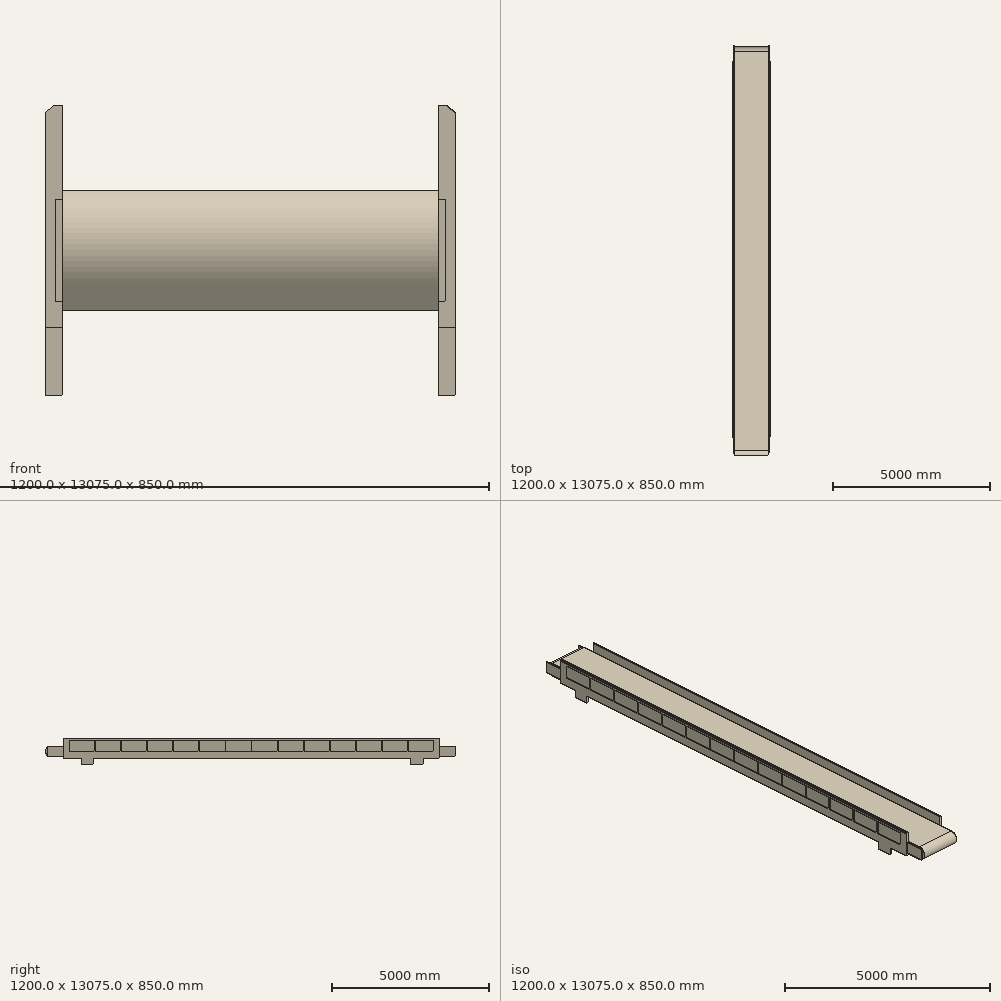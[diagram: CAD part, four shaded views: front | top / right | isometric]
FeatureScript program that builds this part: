
annotation { "Feature Type Name" : "Feature", "Feature Type Description" : "" }
export const myFeature = defineFeature(function(context is Context, id is Id, definition is map)
    precondition{}
    {
        {
            var Q0;
            Q0=qCreatedBy(makeId("Right.planeOp"),FACE);
            cPlane(context, id + "F0", {"entities" : qUnion([Q0]), "cplaneType" : CPlaneType.OFFSET, "offset" : 550 * mm, "width" : 150 * mm, "height" : 150 * mm});
        }
        {
            var Q0;
            Q0=qCreatedBy(makeId("Right.planeOp"),FACE);
            var sketch = newSketch(context, id + "F1", { "sketchPlane" : qUnion([Q0])});
            skCircle(sketch, "E0", {"center": v(0, 0) * mm, "radius": 150 * mm});
            skCircle(sketch, "E1.1.0.0", {"center": v(12700, 0) * mm, "radius": 150 * mm});
            skLineSegment(sketch, "E1.direction1", {"start": v(0, 0) * mm, "end": v(12700, 0) * mm, "construction": true});
            skSolve(sketch);
        }
        {
            var Q0;
            Q0 = qSketchRegion(id + "F1", true);
            var Q1;
            Q1 = qConstructionFilter(qBodyType(qCreatedBy(id + "F1" ,EDGE), BodyType.WIRE), ConstructionObject.NO);
            extrude(context, id + "F2", {"entities" : qUnion([Q0]), "surfaceEntities" : qUnion([Q1]), "depth" : 1100 * mm, "offsetDistance" : 25 * mm});
        }
        {
            var Q0;
            Q0=makeQuery(id+"F2.opExtrude","CAP_FACE",FACE,{"disambiguationData":[OSD([sQuery(id+"F1.wireOp",EDGE,"E0")])],"isStart":false});
            var sketch = newSketch(context, id + "F3", { "sketchPlane" : qUnion([Q0])});
            skCircle(sketch, "E2", {"center": v(0, 0) * mm, "radius": 175 * mm});
            skCircle(sketch, "E3", {"center": v(12700, 0) * mm, "radius": 175 * mm});
            skLineSegment(sketch, "E4.bottom", {"start": v(0, 175) * mm, "end": v(12700, 175) * mm});
            skLineSegment(sketch, "E4.top", {"start": v(0, -175) * mm, "end": v(12700, -175) * mm});
            skLineSegment(sketch, "E4.left", {"start": v(0, 175) * mm, "end": v(0, -175) * mm});
            skLineSegment(sketch, "E4.right", {"start": v(12700, 175) * mm, "end": v(12700, -175) * mm});
            skSolve(sketch);
        }
        {
            var Q0;
            Q0 = qSketchRegion(id + "F3", true);
            extrude(context, id + "F4", {"entities" : qUnion([Q0]), "oppositeDirection" : true, "depth" : 1100 * mm, "offsetDistance" : 25 * mm});
        }
        {
            var Q0;
            Q0=qCreatedBy(makeId("Front.planeOp"),FACE);
            var sketch = newSketch(context, id + "F5", { "sketchPlane" : qUnion([Q0])});
            skLineSegment(sketch, "E5.bottom", {"start": v(0, 425) * mm, "end": v(-25, 425) * mm});
            skLineSegment(sketch, "E5.top", {"start": v(0, -225) * mm, "end": v(-50, -225) * mm});
            skLineSegment(sketch, "E5.left", {"start": v(0, 425) * mm, "end": v(0, -225) * mm});
            skLineSegment(sketch, "E5.right", {"start": v(-50, 401.85) * mm, "end": v(-50, -225) * mm});
            skLineSegment(sketch, "E6", {"start": v(-25, 425) * mm, "end": v(-50, 401.85) * mm});
            skPoint(sketch, "E7.orphan", {"position": v(-50, 425) * mm});
            skLineSegment(sketch, "E8.MirrorCS", {"start": v(1100, 425) * mm, "end": v(1125, 425) * mm});
            skLineSegment(sketch, "E9.MirrorCS", {"start": v(1125, 425) * mm, "end": v(1150, 401.85) * mm});
            skLineSegment(sketch, "E10.MirrorCS", {"start": v(1100, -225) * mm, "end": v(1150, -225) * mm});
            skPoint(sketch, "E11.MirrorP", {"position": v(1150, 425) * mm});
            skLineSegment(sketch, "E12.MirrorCS", {"start": v(1150, 401.85) * mm, "end": v(1150, -225) * mm});
            skLineSegment(sketch, "E13.MirrorCS", {"start": v(1100, 425) * mm, "end": v(1100, -225) * mm});
            skSolve(sketch);
        }
        {
            var Q0;
            Q0 = qSketchRegion(id + "F5", true);
            extrude(context, id + "F6", {"entities" : qUnion([Q0]), "oppositeDirection" : true, "depth" : 12400 * mm, "offsetDistance" : 25 * mm, "hasSecondDirection" : true, "secondDirectionOppositeDirection" : false, "secondDirectionDepth" : -400 * mm});
        }
        {
            var Q0;
            Q0=makeQuery(id+"F6.opExtrude","CAP_FACE",FACE,{"disambiguationData":[OSD([sQuery(id+"F5.wireOp",EDGE,"E5.bottom"),sQuery(id+"F5.wireOp",EDGE,"E5.top"),sQuery(id+"F5.wireOp",EDGE,"E5.left"),sQuery(id+"F5.wireOp",EDGE,"E5.right"),sQuery(id+"F5.wireOp",EDGE,"E6")])],"isStart":true});
            var sketch = newSketch(context, id + "F7", { "sketchPlane" : qUnion([Q0])});
            skLineSegment(sketch, "E14.bottom", {"start": v(0, 150) * mm, "end": v(-20, 150) * mm});
            skLineSegment(sketch, "E14.top", {"start": v(0, -150) * mm, "end": v(-20, -150) * mm});
            skLineSegment(sketch, "E14.left", {"start": v(0, 150) * mm, "end": v(0, -150) * mm});
            skLineSegment(sketch, "E14.right", {"start": v(-20, 150) * mm, "end": v(-20, -150) * mm});
            skLineSegment(sketch, "E15.MirrorCS", {"start": v(1100, -150) * mm, "end": v(1120, -150) * mm});
            skLineSegment(sketch, "E16.MirrorCS", {"start": v(1100, 150) * mm, "end": v(1120, 150) * mm});
            skLineSegment(sketch, "E17.MirrorCS", {"start": v(1120, 150) * mm, "end": v(1120, -150) * mm});
            skLineSegment(sketch, "E18.MirrorCS", {"start": v(1100, 150) * mm, "end": v(1100, -150) * mm});
            skSolve(sketch);
        }
        {
            var Q0;
            Q0 = qSketchRegion(id + "F7", true);
            extrude(context, id + "F8", {"entities" : qUnion([Q0]), "operationType" : NewBodyOperationType.ADD, "depth" : 500 * mm, "offsetDistance" : 25 * mm, "hasSecondDirection" : true, "secondDirectionOppositeDirection" : true, "secondDirectionDepth" : 12500 * mm});
        }
        {
            var Q0;
            Q0=makeQuery(id+"F6.opExtrude","SWEPT_FACE",FACE,{"disambiguationData":[OSD([sQuery(id+"F5.wireOp",EDGE,"E5.right")])]});
            var sketch = newSketch(context, id + "F9", { "sketchPlane" : qUnion([Q0])});
            skLineSegment(sketch, "E19.bottom", {"start": v(-600, 340) * mm, "end": v(-1400, 340) * mm});
            skLineSegment(sketch, "E19.top", {"start": v(-600, 0) * mm, "end": v(-1400, 0) * mm});
            skLineSegment(sketch, "E19.left", {"start": v(-600, 340) * mm, "end": v(-600, 0) * mm});
            skLineSegment(sketch, "E19.right", {"start": v(-1400, 340) * mm, "end": v(-1400, 0) * mm});
            skLineSegment(sketch, "E20.1.0.0", {"start": v(-1430, 0) * mm, "end": v(-2230, 0) * mm});
            skLineSegment(sketch, "E20.1.0.1", {"start": v(-2230, 340) * mm, "end": v(-2230, 0) * mm});
            skLineSegment(sketch, "E20.1.0.2", {"start": v(-1430, 340) * mm, "end": v(-1430, 0) * mm});
            skLineSegment(sketch, "E20.1.0.3", {"start": v(-1430, 340) * mm, "end": v(-2230, 340) * mm});
            skLineSegment(sketch, "E20.2.0.0", {"start": v(-2260, 0) * mm, "end": v(-3060, 0) * mm});
            skLineSegment(sketch, "E20.2.0.1", {"start": v(-3060, 340) * mm, "end": v(-3060, 0) * mm});
            skLineSegment(sketch, "E20.2.0.2", {"start": v(-2260, 340) * mm, "end": v(-2260, 0) * mm});
            skLineSegment(sketch, "E20.2.0.3", {"start": v(-2260, 340) * mm, "end": v(-3060, 340) * mm});
            skLineSegment(sketch, "E20.3.0.0", {"start": v(-3090, 0) * mm, "end": v(-3890, 0) * mm});
            skLineSegment(sketch, "E20.3.0.1", {"start": v(-3890, 340) * mm, "end": v(-3890, 0) * mm});
            skLineSegment(sketch, "E20.3.0.2", {"start": v(-3090, 340) * mm, "end": v(-3090, 0) * mm});
            skLineSegment(sketch, "E20.3.0.3", {"start": v(-3090, 340) * mm, "end": v(-3890, 340) * mm});
            skLineSegment(sketch, "E20.4.0.0", {"start": v(-3920, 0) * mm, "end": v(-4720, 0) * mm});
            skLineSegment(sketch, "E20.4.0.1", {"start": v(-4720, 340) * mm, "end": v(-4720, 0) * mm});
            skLineSegment(sketch, "E20.4.0.2", {"start": v(-3920, 340) * mm, "end": v(-3920, 0) * mm});
            skLineSegment(sketch, "E20.4.0.3", {"start": v(-3920, 340) * mm, "end": v(-4720, 340) * mm});
            skLineSegment(sketch, "E20.5.0.0", {"start": v(-4750, 0) * mm, "end": v(-5550, 0) * mm});
            skLineSegment(sketch, "E20.5.0.1", {"start": v(-5550, 340) * mm, "end": v(-5550, 0) * mm});
            skLineSegment(sketch, "E20.5.0.2", {"start": v(-4750, 340) * mm, "end": v(-4750, 0) * mm});
            skLineSegment(sketch, "E20.5.0.3", {"start": v(-4750, 340) * mm, "end": v(-5550, 340) * mm});
            skLineSegment(sketch, "E20.6.0.0", {"start": v(-5580, 0) * mm, "end": v(-6380, 0) * mm});
            skLineSegment(sketch, "E20.6.0.1", {"start": v(-6380, 340) * mm, "end": v(-6380, 0) * mm});
            skLineSegment(sketch, "E20.6.0.2", {"start": v(-5580, 340) * mm, "end": v(-5580, 0) * mm});
            skLineSegment(sketch, "E20.6.0.3", {"start": v(-5580, 340) * mm, "end": v(-6380, 340) * mm});
            skLineSegment(sketch, "E20.7.0.0", {"start": v(-6410, 0) * mm, "end": v(-7210, 0) * mm});
            skLineSegment(sketch, "E20.7.0.1", {"start": v(-7210, 340) * mm, "end": v(-7210, 0) * mm});
            skLineSegment(sketch, "E20.7.0.2", {"start": v(-6410, 340) * mm, "end": v(-6410, 0) * mm});
            skLineSegment(sketch, "E20.7.0.3", {"start": v(-6410, 340) * mm, "end": v(-7210, 340) * mm});
            skLineSegment(sketch, "E20.8.0.0", {"start": v(-7240, 0) * mm, "end": v(-8040, 0) * mm});
            skLineSegment(sketch, "E20.8.0.1", {"start": v(-8040, 340) * mm, "end": v(-8040, 0) * mm});
            skLineSegment(sketch, "E20.8.0.2", {"start": v(-7240, 340) * mm, "end": v(-7240, 0) * mm});
            skLineSegment(sketch, "E20.8.0.3", {"start": v(-7240, 340) * mm, "end": v(-8040, 340) * mm});
            skLineSegment(sketch, "E20.9.0.0", {"start": v(-8070, 0) * mm, "end": v(-8870, 0) * mm});
            skLineSegment(sketch, "E20.9.0.1", {"start": v(-8870, 340) * mm, "end": v(-8870, 0) * mm});
            skLineSegment(sketch, "E20.9.0.2", {"start": v(-8070, 340) * mm, "end": v(-8070, 0) * mm});
            skLineSegment(sketch, "E20.9.0.3", {"start": v(-8070, 340) * mm, "end": v(-8870, 340) * mm});
            skLineSegment(sketch, "E20.10.0.0", {"start": v(-8900, 0) * mm, "end": v(-9700, 0) * mm});
            skLineSegment(sketch, "E20.10.0.1", {"start": v(-9700, 340) * mm, "end": v(-9700, 0) * mm});
            skLineSegment(sketch, "E20.10.0.2", {"start": v(-8900, 340) * mm, "end": v(-8900, 0) * mm});
            skLineSegment(sketch, "E20.10.0.3", {"start": v(-8900, 340) * mm, "end": v(-9700, 340) * mm});
            skLineSegment(sketch, "E20.11.0.0", {"start": v(-9730, 0) * mm, "end": v(-10530, 0) * mm});
            skLineSegment(sketch, "E20.11.0.1", {"start": v(-10530, 340) * mm, "end": v(-10530, 0) * mm});
            skLineSegment(sketch, "E20.11.0.2", {"start": v(-9730, 340) * mm, "end": v(-9730, 0) * mm});
            skLineSegment(sketch, "E20.11.0.3", {"start": v(-9730, 340) * mm, "end": v(-10530, 340) * mm});
            skLineSegment(sketch, "E20.12.0.0", {"start": v(-10560, 0) * mm, "end": v(-11360, 0) * mm});
            skLineSegment(sketch, "E20.12.0.1", {"start": v(-11360, 340) * mm, "end": v(-11360, 0) * mm});
            skLineSegment(sketch, "E20.12.0.2", {"start": v(-10560, 340) * mm, "end": v(-10560, 0) * mm});
            skLineSegment(sketch, "E20.12.0.3", {"start": v(-10560, 340) * mm, "end": v(-11360, 340) * mm});
            skLineSegment(sketch, "E20.13.0.0", {"start": v(-11390, 0) * mm, "end": v(-12190, 0) * mm});
            skLineSegment(sketch, "E20.13.0.1", {"start": v(-12190, 340) * mm, "end": v(-12190, 0) * mm});
            skLineSegment(sketch, "E20.13.0.2", {"start": v(-11390, 340) * mm, "end": v(-11390, 0) * mm});
            skLineSegment(sketch, "E20.13.0.3", {"start": v(-11390, 340) * mm, "end": v(-12190, 340) * mm});
            skLineSegment(sketch, "E20.direction1", {"start": v(-1400, 0) * mm, "end": v(-2230, 0) * mm, "construction": true});
            skSolve(sketch);
        }
        {
            var Q0;
            Q0 = qSketchRegion(id + "F9", true);
            extrude(context, id + "F10", {"entities" : qUnion([Q0]), "operationType" : NewBodyOperationType.REMOVE, "oppositeDirection" : true, "depth" : 10 * mm, "offsetDistance" : 25 * mm});
        }
        {
            var Q0;
            Q0=makeQuery(id+"F6.opExtrude","SWEPT_FACE",FACE,{"disambiguationData":[OSD([sQuery(id+"F5.wireOp",EDGE,"E12.MirrorCS")])]});
            var sketch = newSketch(context, id + "F11", { "sketchPlane" : qUnion([Q0])});
            skLineSegment(sketch, "E21.0.0", {"start": v(1400, 0) * mm, "end": v(600, 0) * mm});
            skLineSegment(sketch, "E21.0.1", {"start": v(600, 0) * mm, "end": v(600, 340) * mm});
            skLineSegment(sketch, "E21.0.2", {"start": v(600, 340) * mm, "end": v(1400, 340) * mm});
            skLineSegment(sketch, "E21.0.3", {"start": v(1400, 340) * mm, "end": v(1400, 0) * mm});
            skLineSegment(sketch, "E22.0.0", {"start": v(1430, 0) * mm, "end": v(1430, 340) * mm});
            skLineSegment(sketch, "E22.0.1", {"start": v(1430, 340) * mm, "end": v(2230, 340) * mm});
            skLineSegment(sketch, "E22.0.2", {"start": v(2230, 340) * mm, "end": v(2230, 0) * mm});
            skLineSegment(sketch, "E22.0.3", {"start": v(2230, 0) * mm, "end": v(1430, 0) * mm});
            skLineSegment(sketch, "E23.0.0", {"start": v(2260, 0) * mm, "end": v(2260, 340) * mm});
            skLineSegment(sketch, "E23.0.1", {"start": v(2260, 340) * mm, "end": v(3060, 340) * mm});
            skLineSegment(sketch, "E23.0.2", {"start": v(3060, 340) * mm, "end": v(3060, 0) * mm});
            skLineSegment(sketch, "E23.0.3", {"start": v(3060, 0) * mm, "end": v(2260, 0) * mm});
            skLineSegment(sketch, "E24.0.0", {"start": v(3090, 0) * mm, "end": v(3090, 340) * mm});
            skLineSegment(sketch, "E24.0.1", {"start": v(3090, 340) * mm, "end": v(3890, 340) * mm});
            skLineSegment(sketch, "E24.0.2", {"start": v(3890, 340) * mm, "end": v(3890, 0) * mm});
            skLineSegment(sketch, "E24.0.3", {"start": v(3890, 0) * mm, "end": v(3090, 0) * mm});
            skLineSegment(sketch, "E25.0.0", {"start": v(3920, 0) * mm, "end": v(3920, 340) * mm});
            skLineSegment(sketch, "E25.0.1", {"start": v(3920, 340) * mm, "end": v(4720, 340) * mm});
            skLineSegment(sketch, "E25.0.2", {"start": v(4720, 340) * mm, "end": v(4720, 0) * mm});
            skLineSegment(sketch, "E25.0.3", {"start": v(4720, 0) * mm, "end": v(3920, 0) * mm});
            skLineSegment(sketch, "E26.0.0", {"start": v(4750, 0) * mm, "end": v(4750, 340) * mm});
            skLineSegment(sketch, "E26.0.1", {"start": v(4750, 340) * mm, "end": v(5550, 340) * mm});
            skLineSegment(sketch, "E26.0.2", {"start": v(5550, 340) * mm, "end": v(5550, 0) * mm});
            skLineSegment(sketch, "E26.0.3", {"start": v(5550, 0) * mm, "end": v(4750, 0) * mm});
            skLineSegment(sketch, "E27.0.0", {"start": v(5580, 0) * mm, "end": v(5580, 340) * mm});
            skLineSegment(sketch, "E27.0.1", {"start": v(5580, 340) * mm, "end": v(6380, 340) * mm});
            skLineSegment(sketch, "E27.0.2", {"start": v(6380, 340) * mm, "end": v(6380, 0) * mm});
            skLineSegment(sketch, "E27.0.3", {"start": v(6380, 0) * mm, "end": v(5580, 0) * mm});
            skLineSegment(sketch, "E28.0.0", {"start": v(6410, 0) * mm, "end": v(6410, 340) * mm});
            skLineSegment(sketch, "E28.0.1", {"start": v(6410, 340) * mm, "end": v(7210, 340) * mm});
            skLineSegment(sketch, "E28.0.2", {"start": v(7210, 340) * mm, "end": v(7210, 0) * mm});
            skLineSegment(sketch, "E28.0.3", {"start": v(7210, 0) * mm, "end": v(6410, 0) * mm});
            skLineSegment(sketch, "E29.0.0", {"start": v(7240, 0) * mm, "end": v(7240, 340) * mm});
            skLineSegment(sketch, "E29.0.1", {"start": v(7240, 340) * mm, "end": v(8040, 340) * mm});
            skLineSegment(sketch, "E29.0.2", {"start": v(8040, 340) * mm, "end": v(8040, 0) * mm});
            skLineSegment(sketch, "E29.0.3", {"start": v(8040, 0) * mm, "end": v(7240, 0) * mm});
            skLineSegment(sketch, "E30.0.0", {"start": v(8070, 0) * mm, "end": v(8070, 340) * mm});
            skLineSegment(sketch, "E30.0.1", {"start": v(8070, 340) * mm, "end": v(8870, 340) * mm});
            skLineSegment(sketch, "E30.0.2", {"start": v(8870, 340) * mm, "end": v(8870, 0) * mm});
            skLineSegment(sketch, "E30.0.3", {"start": v(8870, 0) * mm, "end": v(8070, 0) * mm});
            skLineSegment(sketch, "E31.0.0", {"start": v(8900, 0) * mm, "end": v(8900, 340) * mm});
            skLineSegment(sketch, "E31.0.1", {"start": v(8900, 340) * mm, "end": v(9700, 340) * mm});
            skLineSegment(sketch, "E31.0.2", {"start": v(9700, 340) * mm, "end": v(9700, 0) * mm});
            skLineSegment(sketch, "E31.0.3", {"start": v(9700, 0) * mm, "end": v(8900, 0) * mm});
            skLineSegment(sketch, "E32.0.0", {"start": v(9730, 0) * mm, "end": v(9730, 340) * mm});
            skLineSegment(sketch, "E32.0.1", {"start": v(9730, 340) * mm, "end": v(10530, 340) * mm});
            skLineSegment(sketch, "E32.0.2", {"start": v(10530, 340) * mm, "end": v(10530, 0) * mm});
            skLineSegment(sketch, "E32.0.3", {"start": v(10530, 0) * mm, "end": v(9730, 0) * mm});
            skLineSegment(sketch, "E33.0.0", {"start": v(10560, 0) * mm, "end": v(10560, 340) * mm});
            skLineSegment(sketch, "E33.0.1", {"start": v(10560, 340) * mm, "end": v(11360, 340) * mm});
            skLineSegment(sketch, "E33.0.2", {"start": v(11360, 340) * mm, "end": v(11360, 0) * mm});
            skLineSegment(sketch, "E33.0.3", {"start": v(11360, 0) * mm, "end": v(10560, 0) * mm});
            skLineSegment(sketch, "E34.0.0", {"start": v(11390, 0) * mm, "end": v(11390, 340) * mm});
            skLineSegment(sketch, "E34.0.1", {"start": v(11390, 340) * mm, "end": v(12190, 340) * mm});
            skLineSegment(sketch, "E34.0.2", {"start": v(12190, 340) * mm, "end": v(12190, 0) * mm});
            skLineSegment(sketch, "E34.0.3", {"start": v(12190, 0) * mm, "end": v(11390, 0) * mm});
            skSolve(sketch);
        }
        {
            var Q0;
            Q0 = qSketchRegion(id + "F11", true);
            extrude(context, id + "F12", {"entities" : qUnion([Q0]), "operationType" : NewBodyOperationType.REMOVE, "oppositeDirection" : true, "depth" : 10 * mm, "offsetDistance" : 25 * mm});
        }
        {
            var Q0;
            Q0=makeQuery(id+"F6.opExtrude","SWEPT_FACE",FACE,{"disambiguationData":[OSD([sQuery(id+"F5.wireOp",EDGE,"E10.MirrorCS")])]});
            var sketch = newSketch(context, id + "F13", { "sketchPlane" : qUnion([Q0])});
            skLineSegment(sketch, "E35.bottom", {"start": v(1150, -971.53) * mm, "end": v(1100, -971.53) * mm});
            skLineSegment(sketch, "E35.top", {"start": v(1150, -1371.53) * mm, "end": v(1100, -1371.53) * mm});
            skLineSegment(sketch, "E35.left", {"start": v(1150, -971.53) * mm, "end": v(1150, -1371.53) * mm});
            skLineSegment(sketch, "E35.right", {"start": v(1100, -971.53) * mm, "end": v(1100, -1371.53) * mm});
            skLineSegment(sketch, "E36.0.1.0", {"start": v(1100, -11471.53) * mm, "end": v(1100, -11871.53) * mm});
            skLineSegment(sketch, "E36.0.1.1", {"start": v(1150, -11471.53) * mm, "end": v(1100, -11471.53) * mm});
            skLineSegment(sketch, "E36.0.1.2", {"start": v(1150, -11871.53) * mm, "end": v(1100, -11871.53) * mm});
            skLineSegment(sketch, "E36.0.1.3", {"start": v(1150, -11471.53) * mm, "end": v(1150, -11871.53) * mm});
            skLineSegment(sketch, "E36.1.0.0", {"start": v(-50, -971.53) * mm, "end": v(-50, -1371.53) * mm});
            skLineSegment(sketch, "E36.1.0.1", {"start": v(0, -971.53) * mm, "end": v(-50, -971.53) * mm});
            skLineSegment(sketch, "E36.1.0.2", {"start": v(0, -1371.53) * mm, "end": v(-50, -1371.53) * mm});
            skLineSegment(sketch, "E36.1.0.3", {"start": v(0, -971.53) * mm, "end": v(0, -1371.53) * mm});
            skLineSegment(sketch, "E36.1.1.0", {"start": v(-50, -11471.53) * mm, "end": v(-50, -11871.53) * mm});
            skLineSegment(sketch, "E36.1.1.1", {"start": v(0, -11471.53) * mm, "end": v(-50, -11471.53) * mm});
            skLineSegment(sketch, "E36.1.1.2", {"start": v(0, -11871.53) * mm, "end": v(-50, -11871.53) * mm});
            skLineSegment(sketch, "E36.1.1.3", {"start": v(0, -11471.53) * mm, "end": v(0, -11871.53) * mm});
            skLineSegment(sketch, "E36.direction1", {"start": v(1100, -1371.53) * mm, "end": v(-50, -1371.53) * mm, "construction": true});
            skLineSegment(sketch, "E36.direction2", {"start": v(1100, -1371.53) * mm, "end": v(1100, -11871.53) * mm, "construction": true});
            skSolve(sketch);
        }
        {
            var Q0;
            Q0 = qSketchRegion(id + "F13", true);
            extrude(context, id + "F14", {"entities" : qUnion([Q0]), "operationType" : NewBodyOperationType.ADD, "depth" : 200 * mm, "offsetDistance" : 25 * mm});
        }
    });
